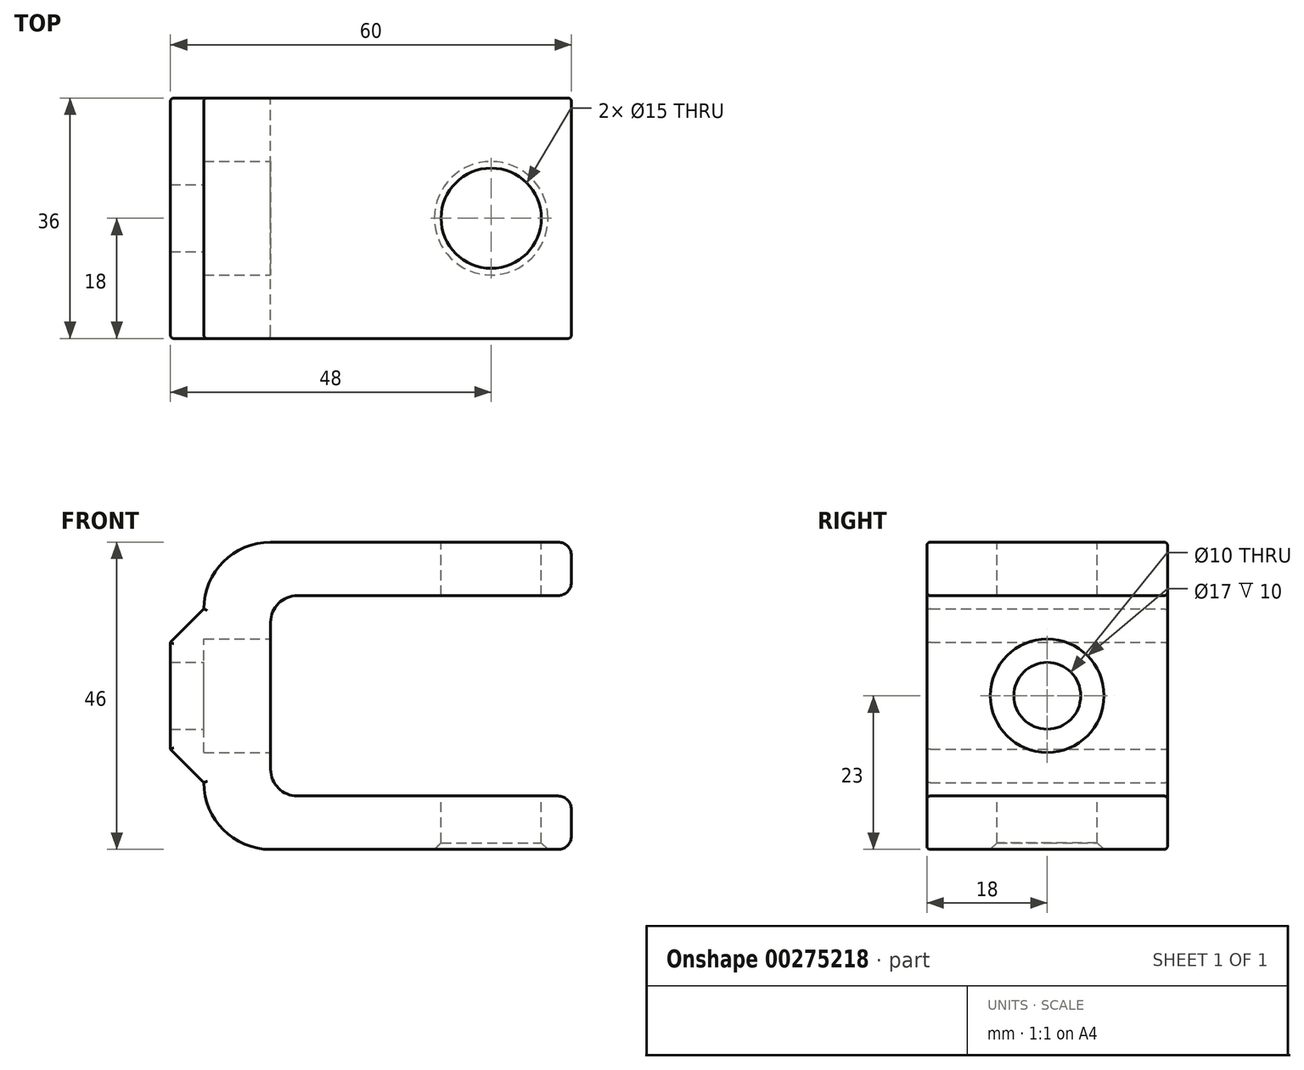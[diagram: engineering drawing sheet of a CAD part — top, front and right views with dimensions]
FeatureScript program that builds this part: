
annotation { "Feature Type Name" : "Feature", "Feature Type Description" : "" }
export const myFeature = defineFeature(function(context is Context, id is Id, definition is map)
    precondition{}
    {
        {
            var Q0;
            Q0=qCreatedBy(makeId("Front.planeOp"),FACE);
            var sketch = newSketch(context, id + "F0", { "sketchPlane" : qUnion([Q0])});
            skLineSegment(sketch, "E0.bottom", {"start": v(28, 23) * mm, "end": v(-15, 23) * mm});
            skLineSegment(sketch, "E0.top", {"start": v(28, -23) * mm, "end": v(-30, -23) * mm});
            skLineSegment(sketch, "E0.left", {"start": v(30, 23) * mm, "end": v(30, -23) * mm, "construction": true});
            skLineSegment(sketch, "E0.right", {"start": v(-30, 23) * mm, "end": v(-30, -23) * mm, "construction": true});
            skPoint(sketch, "E0.middle", {"position": v(0, 0) * mm});
            skLineSegment(sketch, "E1", {"start": v(30, 21) * mm, "end": v(30, 17) * mm});
            skLineSegment(sketch, "E2", {"start": v(28, 15) * mm, "end": v(-11, 15) * mm});
            skLineSegment(sketch, "E3", {"start": v(-15, 11) * mm, "end": v(-15, -15) * mm});
            skLineSegment(sketch, "E4.MirrorCS", {"start": v(28, -15) * mm, "end": v(-11, -15) * mm});
            skLineSegment(sketch, "E5", {"start": v(-30, 8) * mm, "end": v(-25, 13) * mm});
            skLineSegment(sketch, "E6.MirrorCS", {"start": v(-30, -8) * mm, "end": v(-25, -13) * mm});
            skArc(sketch, "E7", {"start": v(-15, 23) * mm, "mid": v(-22.07, 20.07) * mm, "end": v(-25, 13) * mm});
            skArc(sketch, "E8.MirrorCS", {"start": v(-15, -23) * mm, "mid": v(-22.07, -20.07) * mm, "end": v(-25, -13) * mm});
            skPoint(sketch, "E9.visualSharp", {"position": v(-15, 15) * mm});
            skArc(sketch, "E9.filletArc", {"start": v(-11, 15) * mm, "mid": v(-13.83, 13.83) * mm, "end": v(-15, 11) * mm});
            skLineSegment(sketch, "E10", {"start": v(-30, 8) * mm, "end": v(-30, -8) * mm});
            skArc(sketch, "E11.MirrorCS", {"start": v(-11, -15) * mm, "mid": v(-13.83, -13.83) * mm, "end": v(-15, -11) * mm});
            skPoint(sketch, "E12.visualSharp", {"position": v(30, 23) * mm});
            skArc(sketch, "E12.filletArc", {"start": v(30, 21) * mm, "mid": v(29.41, 22.41) * mm, "end": v(28, 23) * mm});
            skLineSegment(sketch, "E13", {"start": v(30, -17) * mm, "end": v(30, -21) * mm});
            skPoint(sketch, "E14.visualSharp", {"position": v(30, -23) * mm});
            skArc(sketch, "E14.filletArc", {"start": v(28, -23) * mm, "mid": v(29.41, -22.41) * mm, "end": v(30, -21) * mm});
            skPoint(sketch, "E15.visualSharp", {"position": v(30, 15) * mm});
            skArc(sketch, "E15.filletArc", {"start": v(28, 15) * mm, "mid": v(29.41, 15.59) * mm, "end": v(30, 17) * mm});
            skPoint(sketch, "E16.visualSharp", {"position": v(30, -15) * mm});
            skArc(sketch, "E16.filletArc", {"start": v(30, -17) * mm, "mid": v(29.41, -15.59) * mm, "end": v(28, -15) * mm});
            skSolve(sketch);
        }
        {
            var Q0;
            Q0=makeQuery(id+"F0.imprint","IMPRINT",FACE,{"disambiguationData":[TD([[makeQuery(id+"F0.imprint","IMPRINT",EDGE,{"derivedFrom":sQuery(id+"F0.wireOp",EDGE,"E0.bottom")}),1.0]])]});
            extrude(context, id + "F1", {"entities" : qUnion([Q0]), "endBound" : BoundingType.SYMMETRIC, "depth" : 36 * mm});
        }
        {
            var Q0;
            Q0=makeQuery(id+"F1.opExtrude","SWEPT_FACE",FACE,{"disambiguationData":[OSD([sQuery(id+"F0.wireOp",EDGE,"E0.bottom")])]});
            var sketch = newSketch(context, id + "F2", { "sketchPlane" : qUnion([Q0])});
            skCircle(sketch, "E17", {"center": v(18, 0) * mm, "radius": 7.5 * mm});
            skSolve(sketch);
        }
        {
            var Q0;
            Q0=makeQuery(id+"F2.imprint","IMPRINT",FACE,{"disambiguationData":[TD([[makeQuery(id+"F2.imprint","IMPRINT",EDGE,{"derivedFrom":sQuery(id+"F2.wireOp",EDGE,"E17")}),1.0]])]});
            extrude(context, id + "F3", {"entities" : qUnion([Q0]), "operationType" : NewBodyOperationType.REMOVE, "endBound" : BoundingType.THROUGH_ALL, "oppositeDirection" : true, "depth" : 25 * mm});
        }
        {
            var Q0;
            Q0=makeQuery(id+"F1.opExtrude","SWEPT_FACE",FACE,{"disambiguationData":[OSD([sQuery(id+"F0.wireOp",EDGE,"E3")])]});
            var sketch = newSketch(context, id + "F4", { "sketchPlane" : qUnion([Q0])});
            skPoint(sketch, "E18", {"position": v(0, 0) * mm});
            skSolve(sketch);
        }
        {
            var Q0;
            Q0=sQuery(id+"F4.wireOp",VERTEX,"E18");
            var Q1;
            Q1=makeQuery(id+"F1.opExtrude","SWEPT_BODY",BODY,{"disambiguationData":[OSD([sQuery(id+"F0.wireOp",EDGE,"E0.bottom"),sQuery(id+"F0.wireOp",EDGE,"E0.top"),sQuery(id+"F0.wireOp",EDGE,"E1"),sQuery(id+"F0.wireOp",EDGE,"E2"),sQuery(id+"F0.wireOp",EDGE,"E3"),sQuery(id+"F0.wireOp",EDGE,"E4.MirrorCS"),sQuery(id+"F0.wireOp",EDGE,"E5"),sQuery(id+"F0.wireOp",EDGE,"E6.MirrorCS"),sQuery(id+"F0.wireOp",EDGE,"E7"),sQuery(id+"F0.wireOp",EDGE,"E8.MirrorCS"),sQuery(id+"F0.wireOp",EDGE,"E9.filletArc"),sQuery(id+"F0.wireOp",EDGE,"E10"),sQuery(id+"F0.wireOp",EDGE,"E11.MirrorCS"),sQuery(id+"F0.wireOp",EDGE,"E12.filletArc"),sQuery(id+"F0.wireOp",EDGE,"E13"),sQuery(id+"F0.wireOp",EDGE,"E14.filletArc"),sQuery(id+"F0.wireOp",EDGE,"E15.filletArc"),sQuery(id+"F0.wireOp",EDGE,"E16.filletArc")])]});
            hole(context, id + "F5", {"style" : HoleStyle.C_BORE, "endStyle" : HoleEndStyle.THROUGH, "holeDiameter" : 10 * mm, "cBoreDiameter" : 17 * mm, "cBoreDepth" : 10 * mm, "tappedDepth" : 12 * mm, "tapClearance" : 3, "locations" : qUnion([Q0]), "scope" : qUnion([Q1])});
        }
        {
            var Q0;
            Q0=makeQuery(id+"F3.boolean.opBoolean","INTERSECT",EDGE,{"derivedFrom":[makeQuery(id+"F1.opExtrude","SWEPT_FACE",FACE,{"disambiguationData":[OSD([sQuery(id+"F0.wireOp",EDGE,"E0.top")])]}),makeQuery(id+"F3.opExtrude","SWEPT_FACE",FACE,{"disambiguationData":[OSD([sQuery(id+"F2.wireOp",EDGE,"E17")])]})]});
            var Q1;
            Q1=makeQuery(id+"F3.boolean.opBoolean","COPY",EDGE,{"derivedFrom":makeQuery(id+"F3.opExtrude","CAP_EDGE",EDGE,{"disambiguationData":[OSD([sQuery(id+"F2.wireOp",EDGE,"E17")])],"isStart":true})});
            var Q2;
            Q2=makeQuery(id+"F5.hole-0.boolean.opBoolean","INTERSECT",EDGE,{"derivedFrom":[makeQuery(id+"F1.opExtrude","SWEPT_FACE",FACE,{"disambiguationData":[OSD([sQuery(id+"F0.wireOp",EDGE,"E10")])]}),makeQuery(id+"F5.hole-0.opRevolve","SWEPT_FACE",FACE,{"disambiguationData":[OSD([sQuery(id+"F5.hole-0.sketch.wireOp",EDGE,"core_line_2")])]})]});
            chamfer(context, id + "F6", {"entities" : qUnion([Q0, Q1, Q2]), "chamferType" : ChamferType.OFFSET_ANGLE, "width" : 1 * mm, "oppositeDirection" : false, "angle" : 45 * degree, "tangentPropagation" : true});
        }
        {
            var Q0;
            Q0=makeQuery(id+"F1.opExtrude","CAP_FACE",FACE,{"disambiguationData":[OSD([sQuery(id+"F0.wireOp",EDGE,"E0.bottom"),sQuery(id+"F0.wireOp",EDGE,"E0.top"),sQuery(id+"F0.wireOp",EDGE,"E1"),sQuery(id+"F0.wireOp",EDGE,"E2"),sQuery(id+"F0.wireOp",EDGE,"E3"),sQuery(id+"F0.wireOp",EDGE,"E4.MirrorCS"),sQuery(id+"F0.wireOp",EDGE,"E5"),sQuery(id+"F0.wireOp",EDGE,"E6.MirrorCS"),sQuery(id+"F0.wireOp",EDGE,"E7"),sQuery(id+"F0.wireOp",EDGE,"E8.MirrorCS"),sQuery(id+"F0.wireOp",EDGE,"E9.filletArc"),sQuery(id+"F0.wireOp",EDGE,"E10"),sQuery(id+"F0.wireOp",EDGE,"E11.MirrorCS"),sQuery(id+"F0.wireOp",EDGE,"E12.filletArc"),sQuery(id+"F0.wireOp",EDGE,"E13"),sQuery(id+"F0.wireOp",EDGE,"E14.filletArc"),sQuery(id+"F0.wireOp",EDGE,"E15.filletArc"),sQuery(id+"F0.wireOp",EDGE,"E16.filletArc")])],"isStart":true});
            var Q1;
            Q1=makeQuery(id+"F1.opExtrude","CAP_FACE",FACE,{"disambiguationData":[OSD([sQuery(id+"F0.wireOp",EDGE,"E0.bottom"),sQuery(id+"F0.wireOp",EDGE,"E0.top"),sQuery(id+"F0.wireOp",EDGE,"E1"),sQuery(id+"F0.wireOp",EDGE,"E2"),sQuery(id+"F0.wireOp",EDGE,"E3"),sQuery(id+"F0.wireOp",EDGE,"E4.MirrorCS"),sQuery(id+"F0.wireOp",EDGE,"E5"),sQuery(id+"F0.wireOp",EDGE,"E6.MirrorCS"),sQuery(id+"F0.wireOp",EDGE,"E7"),sQuery(id+"F0.wireOp",EDGE,"E8.MirrorCS"),sQuery(id+"F0.wireOp",EDGE,"E9.filletArc"),sQuery(id+"F0.wireOp",EDGE,"E10"),sQuery(id+"F0.wireOp",EDGE,"E11.MirrorCS"),sQuery(id+"F0.wireOp",EDGE,"E12.filletArc"),sQuery(id+"F0.wireOp",EDGE,"E13"),sQuery(id+"F0.wireOp",EDGE,"E14.filletArc"),sQuery(id+"F0.wireOp",EDGE,"E15.filletArc"),sQuery(id+"F0.wireOp",EDGE,"E16.filletArc")])],"isStart":false});
            fillet(context, id + "F7", {"entities" : qUnion([Q0, Q1]), "radius" : .5 * mm, "tangentPropagation" : true, "allowEdgeOverflow" : false});
        }
    });
